# Revit family: sh-5404
name_source: partatom
category: Lighting Fixtures
revit_build: Autodesk Revit 2017 (Build: 20160225_1515(x64)
units: mm (PartAtom-declared; Revit-internal decimal feet)

## family parameters
Always vertical = Yes
Cut with Voids When Loaded = No
Host = Wall
Light Source = No
OmniClass Number = 23.80.70.00
OmniClass Title = Lighting
Part Type = Normal
Room Calculation Point = No
Round Connector Dimension = Use Diameter
Shared = Yes

## types (1)
- SH-5404(Black body-3000K-LED)
    Body Material = Aluminum
    Body color = Graphite color
    Cost = 0 $
    Diffuser Material = polycarbonate-anti uv
    Height = 24.7 cm
    IP = IP54
    Lamp = LED
    Manufacturer = SHOA
    Model = SH-5404
    Protection Class = class I
    Type medule = SMD-DOB
    URL = https://www.shoaco.com
    Voltage/Frequency = 230 V Ac/50HZ
    Website = www.shoaco.com
    color temperature = 3000K
    consumption current = 0 A
    instalation = Wall Mounted
    wattage. = 9 W

## geometry (parser evidence)
native form markers: Sweep x5
no freeform markers — native parametric forms only
